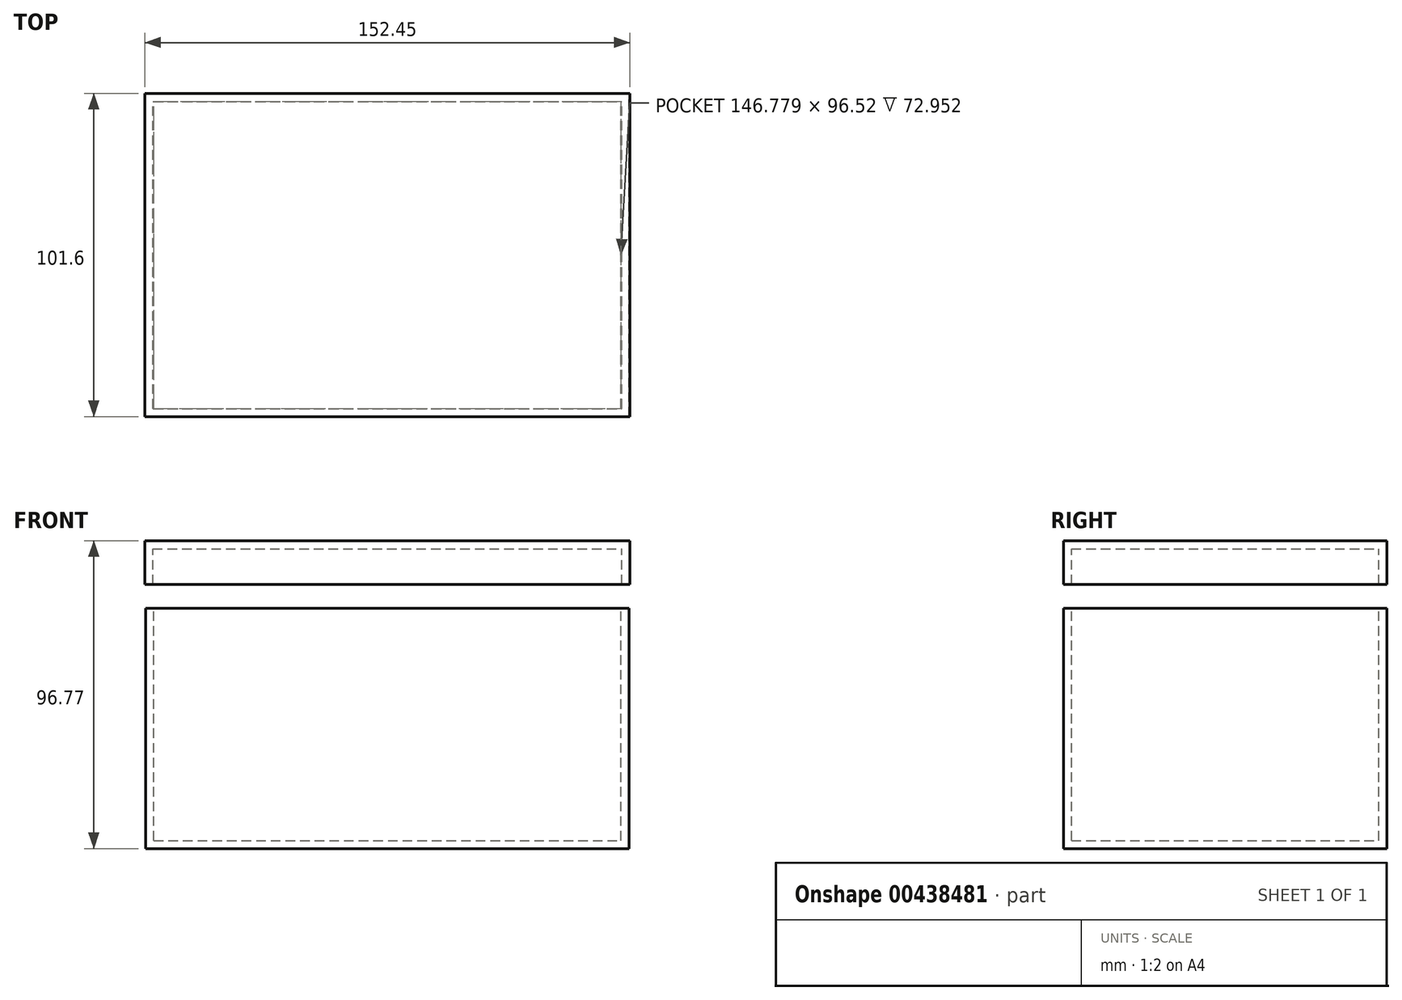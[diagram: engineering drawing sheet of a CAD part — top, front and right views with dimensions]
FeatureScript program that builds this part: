
annotation { "Feature Type Name" : "Feature", "Feature Type Description" : "" }
export const myFeature = defineFeature(function(context is Context, id is Id, definition is map)
    precondition{}
    {
        {
            var Q0;
            Q0=qCreatedBy(makeId("Front.planeOp"),FACE);
            var sketch = newSketch(context, id + "F0", { "sketchPlane" : qUnion([Q0])});
            skLineSegment(sketch, "E0.bottom", {"start": v(-75.78, -59.02) * mm, "end": v(76.08, -59.02) * mm});
            skLineSegment(sketch, "E0.top", {"start": v(-75.78, 16.47) * mm, "end": v(76.08, 16.47) * mm});
            skLineSegment(sketch, "E0.left", {"start": v(-75.78, -59.02) * mm, "end": v(-75.78, 16.47) * mm});
            skLineSegment(sketch, "E0.right", {"start": v(76.08, -59.02) * mm, "end": v(76.08, 16.47) * mm});
            skSolve(sketch);
        }
        {
            var Q0;
            Q0=makeQuery(id+"F0.imprint","IMPRINT",FACE,{"disambiguationData":[TD([[makeQuery(id+"F0.imprint","IMPRINT",EDGE,{"derivedFrom":sQuery(id+"F0.wireOp",EDGE,"E0.bottom")}),1.0]])]});
            extrude(context, id + "F1", {"entities" : qUnion([Q0]), "depth" : 101.6 * mm});
        }
        {
            var Q0;
            Q0=makeQuery(id+"F1.opExtrude","SWEPT_FACE",FACE,{"disambiguationData":[OSD([sQuery(id+"F0.wireOp",EDGE,"E0.top")])]});
            shell(context, id + "F2", {"entities" : qUnion([Q0]), "thickness" : 2.54 * mm});
        }
        {
            var Q0;
            Q0=qCreatedBy(makeId("Front.planeOp"),FACE);
            var sketch = newSketch(context, id + "F3", { "sketchPlane" : qUnion([Q0])});
            skLineSegment(sketch, "E1.bottom", {"start": v(-76.08, 24.05) * mm, "end": v(76.37, 24.05) * mm});
            skLineSegment(sketch, "E1.top", {"start": v(-76.08, 37.75) * mm, "end": v(76.37, 37.75) * mm});
            skLineSegment(sketch, "E1.left", {"start": v(-76.08, 24.05) * mm, "end": v(-76.08, 37.75) * mm});
            skLineSegment(sketch, "E1.right", {"start": v(76.37, 24.05) * mm, "end": v(76.37, 37.75) * mm});
            skSolve(sketch);
        }
        {
            var Q0;
            Q0=makeQuery(id+"F3.imprint","IMPRINT",FACE,{"disambiguationData":[TD([[makeQuery(id+"F3.imprint","IMPRINT",EDGE,{"derivedFrom":sQuery(id+"F3.wireOp",EDGE,"E1.bottom")}),1.0]])]});
            extrude(context, id + "F4", {"entities" : qUnion([Q0]), "depth" : 101.6 * mm});
        }
        {
            var Q0;
            Q0=makeQuery(id+"F4.opExtrude","SWEPT_FACE",FACE,{"disambiguationData":[OSD([sQuery(id+"F3.wireOp",EDGE,"E1.bottom")])]});
            shell(context, id + "F5", {"entities" : qUnion([Q0]), "thickness" : 2.54 * mm});
        }
    });
